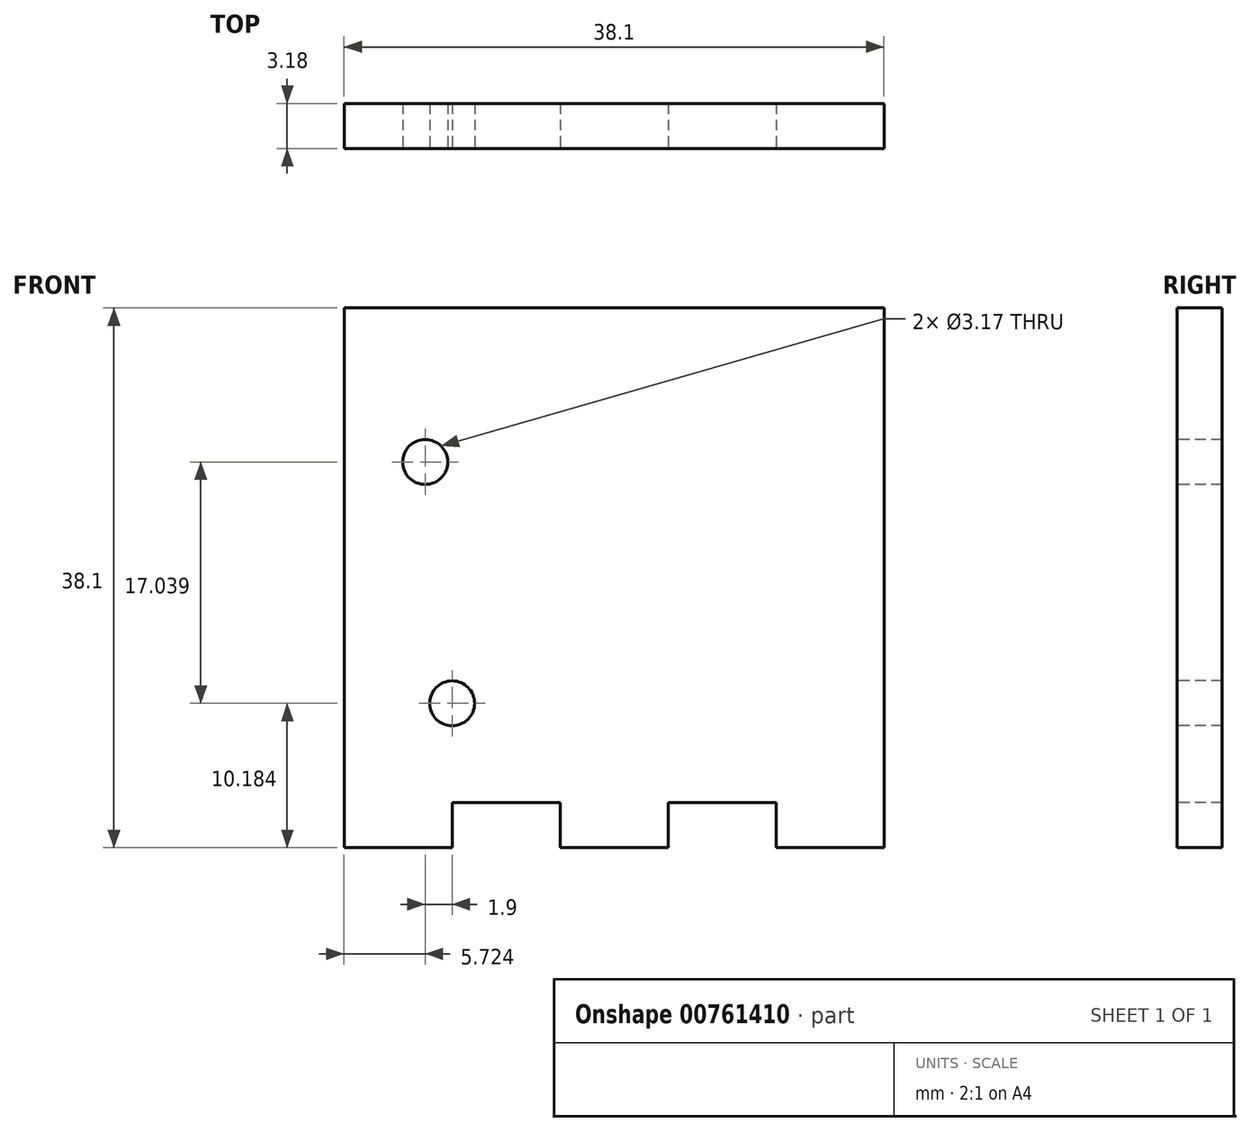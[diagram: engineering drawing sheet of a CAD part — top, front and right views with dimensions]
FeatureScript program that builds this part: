
annotation { "Feature Type Name" : "Feature", "Feature Type Description" : "" }
export const myFeature = defineFeature(function(context is Context, id is Id, definition is map)
    precondition{}
    {
        {
            var Q0;
            Q0=qCreatedBy(makeId("Front.planeOp"),FACE);
            var sketch = newSketch(context, id + "F0", { "sketchPlane" : qUnion([Q0])});
            skPoint(sketch, "E0.middle", {"position": v(0, 0) * mm});
            skLineSegment(sketch, "E1.bottom", {"start": v(-25.26, 16.76) * mm, "end": v(12.84, 16.76) * mm});
            skLineSegment(sketch, "E1.top", {"start": v(-25.26, -21.34) * mm, "end": v(12.84, -21.34) * mm});
            skLineSegment(sketch, "E1.left", {"start": v(-25.26, 16.76) * mm, "end": v(-25.26, -21.34) * mm});
            skLineSegment(sketch, "E1.right", {"start": v(12.84, 16.76) * mm, "end": v(12.84, -21.34) * mm});
            skSolve(sketch);
        }
        {
            var Q0;
            Q0=qSketchRegion(id+"F0",true);
            extrude(context, id + "F1", {"entities" : qUnion([Q0]), "depth" : 3.17 * mm, "offsetDistance" : 25.4 * mm});
        }
        {
            var Q0;
            Q0=makeQuery(id+"F1.opExtrude","CAP_FACE",FACE,{"disambiguationData":[OSD([sQuery(id+"F0.wireOp",EDGE,"E1.bottom"),sQuery(id+"F0.wireOp",EDGE,"E1.top"),sQuery(id+"F0.wireOp",EDGE,"E1.left"),sQuery(id+"F0.wireOp",EDGE,"E1.right")])],"isStart":false});
            var sketch = newSketch(context, id + "F2", { "sketchPlane" : qUnion([Q0])});
            skLineSegment(sketch, "E2.bottom", {"start": v(-25.26, 16.76) * mm, "end": v(12.84, 16.76) * mm});
            skLineSegment(sketch, "E2.top", {"start": v(-25.26, -21.34) * mm, "end": v(12.84, -21.34) * mm});
            skLineSegment(sketch, "E2.left", {"start": v(-25.26, 19.3) * mm, "end": v(-25.26, -21.34) * mm});
            skLineSegment(sketch, "E2.right", {"start": v(12.84, 16.76) * mm, "end": v(12.84, -21.34) * mm});
            skArc(sketch, "E3", {"start": v(-0.8, 3.39) * mm, "mid": v(11.57, 5.4) * mm, "end": v(-0.8, 7.43) * mm});
            skArc(sketch, "E4", {"start": v(-0.8, 7.43) * mm, "mid": v(-4.88, 5.4) * mm, "end": v(-0.8, 3.39) * mm});
            skCircle(sketch, "E5", {"center": v(-19.54, 5.88) * mm, "radius": 1.59 * mm});
            skCircle(sketch, "E6", {"center": v(-17.64, -11.16) * mm, "radius": 1.59 * mm});
            skLineSegment(sketch, "E7.bottom", {"start": v(-25.26, -18.16) * mm, "end": v(-17.64, -18.16) * mm});
            skLineSegment(sketch, "E7.top", {"start": v(-25.26, -21.34) * mm, "end": v(-17.64, -21.34) * mm});
            skLineSegment(sketch, "E7.left", {"start": v(-25.26, -18.16) * mm, "end": v(-25.26, -21.34) * mm});
            skLineSegment(sketch, "E7.right", {"start": v(-17.64, -18.16) * mm, "end": v(-17.64, -21.34) * mm});
            skLineSegment(sketch, "E8.bottom", {"start": v(-10.02, -18.16) * mm, "end": v(-2.4, -18.16) * mm});
            skLineSegment(sketch, "E8.top", {"start": v(-10.02, -21.34) * mm, "end": v(-2.4, -21.34) * mm});
            skLineSegment(sketch, "E8.left", {"start": v(-10.02, -18.16) * mm, "end": v(-10.02, -21.34) * mm});
            skLineSegment(sketch, "E8.right", {"start": v(-2.4, -18.16) * mm, "end": v(-2.4, -21.34) * mm});
            skLineSegment(sketch, "E9.bottom", {"start": v(5.22, -18.16) * mm, "end": v(12.84, -18.16) * mm});
            skLineSegment(sketch, "E9.top", {"start": v(5.22, -21.34) * mm, "end": v(12.84, -21.34) * mm});
            skLineSegment(sketch, "E9.left", {"start": v(5.22, -18.16) * mm, "end": v(5.22, -21.34) * mm});
            skLineSegment(sketch, "E9.right", {"start": v(12.84, -18.16) * mm, "end": v(12.84, -21.34) * mm});
            skLineSegment(sketch, "E10", {"start": v(-17.64, -18.16) * mm, "end": v(-10.02, -18.16) * mm});
            skLineSegment(sketch, "E11", {"start": v(-2.4, -18.16) * mm, "end": v(5.22, -18.16) * mm});
            skSolve(sketch);
        }
        {
            var Q0;
            {var subQ0=sQuery(id+"F2.wireOp",EDGE,"E7.right");Q0=makeQuery(id+"F2.imprint","IMPRINT",FACE,{"disambiguationData":[TD([[makeQuery(id+"F2.imprint","IMPRINT",EDGE,{"derivedFrom":subQ0}),1.0]])]});}
            var Q1;
            {var subQ2=sQuery(id+"F2.wireOp",EDGE,"E8.right");Q1=makeQuery(id+"F2.imprint","IMPRINT",FACE,{"disambiguationData":[TD([[makeQuery(id+"F2.imprint","IMPRINT",EDGE,{"derivedFrom":subQ2}),1.0]])]});}
            var Q2;
            Q2=makeQuery(id+"F2.imprint","IMPRINT",FACE,{"disambiguationData":[TD([[makeQuery(id+"F2.imprint","IMPRINT",EDGE,{"derivedFrom":sQuery(id+"F2.wireOp",EDGE,"E5")}),1.0]])]});
            var Q3;
            Q3=makeQuery(id+"F2.imprint","IMPRINT",FACE,{"disambiguationData":[TD([[makeQuery(id+"F2.imprint","IMPRINT",EDGE,{"derivedFrom":sQuery(id+"F2.wireOp",EDGE,"E6")}),1.0]])]});
            extrude(context, id + "F3", {"entities" : qUnion([Q0, Q1, Q2, Q3]), "operationType" : NewBodyOperationType.REMOVE, "oppositeDirection" : true, "depth" : 3.17 * mm, "offsetDistance" : 25.4 * mm});
        }
        {
            var Q0;
            Q0=makeQuery(id+"F2.imprint","IMPRINT",FACE,{"disambiguationData":[TD([[makeQuery(id+"F2.imprint","IMPRINT",EDGE,{"derivedFrom":sQuery(id+"F2.wireOp",EDGE,"E6")}),1.0]])]});
            var Q1;
            Q1=makeQuery(id+"F2.imprint","IMPRINT",FACE,{"disambiguationData":[TD([[makeQuery(id+"F2.imprint","IMPRINT",EDGE,{"derivedFrom":sQuery(id+"F2.wireOp",EDGE,"E5")}),1.0]])]});
            extrude(context, id + "F4", {"entities" : qUnion([Q0, Q1]), "operationType" : NewBodyOperationType.REMOVE, "oppositeDirection" : true, "depth" : 2.54 * mm, "offsetDistance" : 25.4 * mm});
        }
    });
